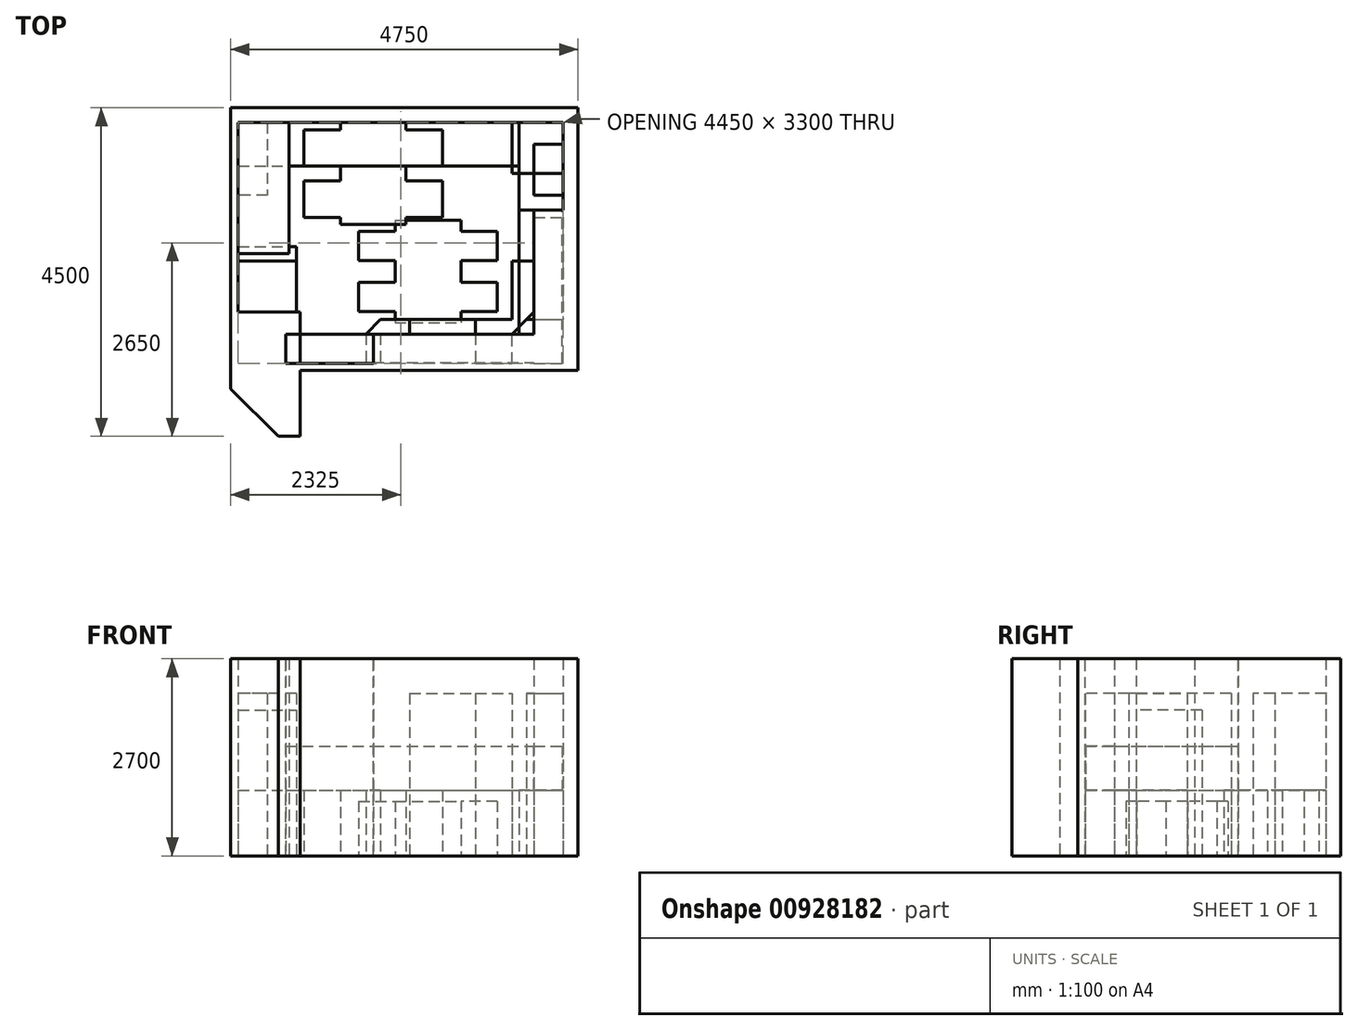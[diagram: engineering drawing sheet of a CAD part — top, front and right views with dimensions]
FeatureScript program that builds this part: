
annotation { "Feature Type Name" : "Feature", "Feature Type Description" : "" }
export const myFeature = defineFeature(function(context is Context, id is Id, definition is map)
    precondition{}
    {
        {
            var Q0;
            Q0=qCreatedBy(makeId("Top.planeOp"),FACE);
            var sketch = newSketch(context, id + "F0", { "sketchPlane" : qUnion([Q0])});
            skLineSegment(sketch, "E0", {"start": v(-2225, 1641.97) * mm, "end": v(2225, 1641.97) * mm});
            skLineSegment(sketch, "E1", {"start": v(2225, 1641.97) * mm, "end": v(2225, -1658.03) * mm});
            skLineSegment(sketch, "E2", {"start": v(-2225, -958.03) * mm, "end": v(-2225, 1641.97) * mm});
            skLineSegment(sketch, "E3.bottom", {"start": v(-2325, 1841.97) * mm, "end": v(2425, 1841.97) * mm});
            skLineSegment(sketch, "E3.left", {"start": v(-2325, 1841.97) * mm, "end": v(-2325, -2008.03) * mm});
            skLineSegment(sketch, "E3.right", {"start": v(2425, 1841.97) * mm, "end": v(2425, -1758.03) * mm});
            skLineSegment(sketch, "E4", {"start": v(-2225, -958.03) * mm, "end": v(-1375, -958.03) * mm});
            skLineSegment(sketch, "E5", {"start": v(-1375, -958.03) * mm, "end": v(-1375, -2658.03) * mm});
            skLineSegment(sketch, "E6", {"start": v(-2325, -2008.03) * mm, "end": v(-1675, -2658.03) * mm});
            skLineSegment(sketch, "E7", {"start": v(-1375, -2658.03) * mm, "end": v(-1675, -2658.03) * mm});
            skLineSegment(sketch, "E8", {"start": v(2425, -1758.03) * mm, "end": v(-1375, -1758.03) * mm});
            skLineSegment(sketch, "E9", {"start": v(2225, -1658.03) * mm, "end": v(-1375, -1658.03) * mm});
            skSolve(sketch);
        }
        {
            var Q0;
            Q0=makeQuery(id+"F0.imprint","IMPRINT",FACE,{"disambiguationData":[TD([[makeQuery(id+"F0.imprint","IMPRINT",EDGE,{"derivedFrom":sQuery(id+"F0.wireOp",EDGE,"E0")}),1.0]])]});
            extrude(context, id + "F1", {"entities" : qUnion([Q0]), "depth" : 2700 * mm, "offsetDistance" : 25 * mm});
        }
        {
            var Q0;
            Q0=makeQuery(id+"F1.opExtrude","SWEPT_FACE",FACE,{"disambiguationData":[OSD([sQuery(id+"F0.wireOp",EDGE,"E0")])]});
            var sketch = newSketch(context, id + "F2", { "sketchPlane" : qUnion([Q0])});
            skLineSegment(sketch, "E10", {"start": v(-2225, 2700) * mm, "end": v(-1525, 2700) * mm});
            skLineSegment(sketch, "E11", {"start": v(-1525, 2700) * mm, "end": v(-1525, 0) * mm});
            skLineSegment(sketch, "E12", {"start": v(-1525, 0) * mm, "end": v(-2225, 0) * mm});
            skLineSegment(sketch, "E13", {"start": v(-2225, 0) * mm, "end": v(-2225, 2700) * mm});
            skSolve(sketch);
        }
        {
            var Q0;
            Q0=makeQuery(id+"F2.imprint","IMPRINT",FACE,{"disambiguationData":[TD([[makeQuery(id+"F2.imprint","IMPRINT",EDGE,{"derivedFrom":sQuery(id+"F2.wireOp",EDGE,"E10")}),-1.0]])]});
            extrude(context, id + "F3", {"entities" : qUnion([Q0]), "depth" : 1800 * mm, "offsetDistance" : 25 * mm});
        }
        {
            var Q0;
            Q0=qCreatedBy(makeId("Top.planeOp"),FACE);
            var sketch = newSketch(context, id + "F4", { "sketchPlane" : qUnion([Q0])});
            skLineSegment(sketch, "E14.bottom", {"start": v(-75, 300) * mm, "end": v(825, 300) * mm});
            skLineSegment(sketch, "E14.left", {"start": v(-75, 300) * mm, "end": v(-75, -1100) * mm});
            skLineSegment(sketch, "E14.right", {"start": v(825, 300) * mm, "end": v(825, -1100) * mm});
            skLineSegment(sketch, "E15", {"start": v(-75, -1100) * mm, "end": v(825, -1100) * mm});
            skLineSegment(sketch, "E16", {"start": v(-75, 150) * mm, "end": v(-575, 150) * mm});
            skLineSegment(sketch, "E17", {"start": v(-575, 150) * mm, "end": v(-575, -250) * mm});
            skLineSegment(sketch, "E18", {"start": v(-575, -250) * mm, "end": v(-75, -250) * mm});
            skLineSegment(sketch, "E19", {"start": v(-75, -550) * mm, "end": v(-575, -550) * mm});
            skLineSegment(sketch, "E20", {"start": v(-575, -550) * mm, "end": v(-575, -950) * mm});
            skLineSegment(sketch, "E21", {"start": v(-575, -950) * mm, "end": v(-75, -950) * mm});
            skLineSegment(sketch, "E22", {"start": v(825, 150) * mm, "end": v(1325, 150) * mm});
            skLineSegment(sketch, "E23", {"start": v(1325, 150) * mm, "end": v(1325, -250) * mm});
            skLineSegment(sketch, "E24", {"start": v(1325, -250) * mm, "end": v(825, -250) * mm});
            skLineSegment(sketch, "E25", {"start": v(825, -550) * mm, "end": v(1325, -550) * mm});
            skLineSegment(sketch, "E26", {"start": v(1325, -550) * mm, "end": v(1325, -950) * mm});
            skLineSegment(sketch, "E27", {"start": v(1325, -950) * mm, "end": v(825, -950) * mm});
            skLineSegment(sketch, "E28", {"start": v(-75, -400) * mm, "end": v(825, -400) * mm});
            skSolve(sketch);
        }
        {
            var Q0;
            {var subQ0=sQuery(id+"F4.wireOp",EDGE,"E16");Q0=makeQuery(id+"F4.imprint","IMPRINT",FACE,{"disambiguationData":[TD([[makeQuery(id+"F4.imprint","IMPRINT",EDGE,{"derivedFrom":subQ0}),1.0]])]});}
            var Q1;
            {var subQ4=sQuery(id+"F4.wireOp",EDGE,"E14.bottom");Q1=makeQuery(id+"F4.imprint","IMPRINT",FACE,{"disambiguationData":[TD([[makeQuery(id+"F4.imprint","IMPRINT",EDGE,{"derivedFrom":subQ4}),-1.0]])]});}
            var Q2;
            {var subQ0=sQuery(id+"F4.wireOp",EDGE,"E22");Q2=makeQuery(id+"F4.imprint","IMPRINT",FACE,{"disambiguationData":[TD([[makeQuery(id+"F4.imprint","IMPRINT",EDGE,{"derivedFrom":subQ0}),-1.0]])]});}
            var Q3;
            {var subQ0=sQuery(id+"F4.wireOp",EDGE,"E15");Q3=makeQuery(id+"F4.imprint","IMPRINT",FACE,{"disambiguationData":[TD([[makeQuery(id+"F4.imprint","IMPRINT",EDGE,{"derivedFrom":subQ0}),1.0]])]});}
            var Q4;
            {var subQ0=sQuery(id+"F4.wireOp",EDGE,"E19");Q4=makeQuery(id+"F4.imprint","IMPRINT",FACE,{"disambiguationData":[TD([[makeQuery(id+"F4.imprint","IMPRINT",EDGE,{"derivedFrom":subQ0}),1.0]])]});}
            var Q5;
            {var subQ0=sQuery(id+"F4.wireOp",EDGE,"E25");Q5=makeQuery(id+"F4.imprint","IMPRINT",FACE,{"disambiguationData":[TD([[makeQuery(id+"F4.imprint","IMPRINT",EDGE,{"derivedFrom":subQ0}),-1.0]])]});}
            extrude(context, id + "F5", {"entities" : qUnion([Q0, Q1, Q2, Q3, Q4, Q5]), "depth" : 750 * mm, "offsetDistance" : 25 * mm});
        }
        {
            var Q0;
            Q0=makeQuery(id+"F1.opExtrude","SWEPT_FACE",FACE,{"disambiguationData":[OSD([sQuery(id+"F0.wireOp",EDGE,"E0")])]});
            var sketch = newSketch(context, id + "F6", { "sketchPlane" : qUnion([Q0])});
            skLineSegment(sketch, "E29.bottom", {"start": v(2225, 900) * mm, "end": v(1625, 900) * mm});
            skLineSegment(sketch, "E29.top", {"start": v(2225, 0) * mm, "end": v(1625, 0) * mm});
            skLineSegment(sketch, "E29.left", {"start": v(2225, 900) * mm, "end": v(2225, 0) * mm});
            skLineSegment(sketch, "E29.right", {"start": v(1625, 900) * mm, "end": v(1625, 0) * mm});
            skSolve(sketch);
        }
        {
            var Q0;
            Q0=makeQuery(id+"F6.imprint","IMPRINT",FACE,{"disambiguationData":[TD([[makeQuery(id+"F6.imprint","IMPRINT",EDGE,{"derivedFrom":sQuery(id+"F6.wireOp",EDGE,"E29.bottom")}),1.0]])]});
            extrude(context, id + "F7", {"entities" : qUnion([Q0]), "depth" : 1200 * mm, "offsetDistance" : 25 * mm});
        }
        {
            var Q0;
            Q0=makeQuery(id+"F7.opExtrude","CAP_FACE",FACE,{"disambiguationData":[OSD([sQuery(id+"F6.wireOp",EDGE,"E29.bottom"),sQuery(id+"F6.wireOp",EDGE,"E29.top"),sQuery(id+"F6.wireOp",EDGE,"E29.left"),sQuery(id+"F6.wireOp",EDGE,"E29.right")])],"isStart":false});
            var sketch = newSketch(context, id + "F8", { "sketchPlane" : qUnion([Q0])});
            skLineSegment(sketch, "E30", {"start": v(2225, 0) * mm, "end": v(2225, 2700) * mm});
            skLineSegment(sketch, "E31", {"start": v(2225, 2700) * mm, "end": v(1825, 2700) * mm});
            skLineSegment(sketch, "E32", {"start": v(1825, 2700) * mm, "end": v(1825, 1500) * mm});
            skLineSegment(sketch, "E33", {"start": v(1825, 1500) * mm, "end": v(2215, 1500) * mm});
            skLineSegment(sketch, "E34", {"start": v(2215, 1500) * mm, "end": v(2215, 900) * mm});
            skLineSegment(sketch, "E35", {"start": v(2215, 900) * mm, "end": v(1625, 900) * mm});
            skLineSegment(sketch, "E36", {"start": v(1625, 900) * mm, "end": v(1625, 0) * mm});
            skLineSegment(sketch, "E37", {"start": v(1625, 0) * mm, "end": v(2225, 0) * mm});
            skSolve(sketch);
        }
        {
            var Q0;
            {var subQ0=sQuery(id+"F8.wireOp",EDGE,"E31");Q0=makeQuery(id+"F8.imprint","IMPRINT",FACE,{"disambiguationData":[TD([[makeQuery(id+"F8.imprint","IMPRINT",EDGE,{"derivedFrom":subQ0}),1.0]])]});}
            var Q1;
            {var subQ1=sQuery(id+"F8.wireOp",EDGE,"E35");Q1=makeQuery(id+"F8.imprint","IMPRINT",FACE,{"disambiguationData":[TD([[makeQuery(id+"F8.imprint","IMPRINT",EDGE,{"derivedFrom":subQ1}),1.0]])]});}
            extrude(context, id + "F9", {"entities" : qUnion([Q0, Q1]), "endBound" : BoundingType.UP_TO_NEXT, "depth" : 25 * mm, "offsetDistance" : 25 * mm});
        }
        {
            var Q0;
            Q0=makeQuery(id+"F9.opExtrude","SWEPT_FACE",FACE,{"disambiguationData":[OSD([sQuery(id+"F8.wireOp",EDGE,"E36")])]});
            var sketch = newSketch(context, id + "F10", { "sketchPlane" : qUnion([Q0])});
            skLineSegment(sketch, "E38", {"start": v(1658.03, 0) * mm, "end": v(1658.03, 2700) * mm});
            skLineSegment(sketch, "E39", {"start": v(1658.03, 2700) * mm, "end": v(1258.03, 2700) * mm});
            skLineSegment(sketch, "E40", {"start": v(1258.03, 2700) * mm, "end": v(1258.03, 1500) * mm});
            skLineSegment(sketch, "E41", {"start": v(1258.03, 1500) * mm, "end": v(1648.03, 1500) * mm});
            skLineSegment(sketch, "E42", {"start": v(1648.03, 1500) * mm, "end": v(1648.03, 900) * mm});
            skLineSegment(sketch, "E43", {"start": v(1648.03, 900) * mm, "end": v(1258.03, 900) * mm});
            skLineSegment(sketch, "E44", {"start": v(1258.03, 900) * mm, "end": v(1258.03, 0) * mm});
            skLineSegment(sketch, "E45", {"start": v(1258.03, 0) * mm, "end": v(1658.03, 0) * mm});
            skSolve(sketch);
        }
        {
            var Q0;
            {var subQ0=sQuery(id+"F10.wireOp",EDGE,"E39");Q0=makeQuery(id+"F10.imprint","IMPRINT",FACE,{"disambiguationData":[TD([[makeQuery(id+"F10.imprint","IMPRINT",EDGE,{"derivedFrom":subQ0}),1.0]])]});}
            var Q1;
            {var subQ1=sQuery(id+"F10.wireOp",EDGE,"E43");Q1=makeQuery(id+"F10.imprint","IMPRINT",FACE,{"disambiguationData":[TD([[makeQuery(id+"F10.imprint","IMPRINT",EDGE,{"derivedFrom":subQ1}),1.0]])]});}
            extrude(context, id + "F11", {"entities" : qUnion([Q0, Q1]), "operationType" : NewBodyOperationType.ADD, "depth" : 2000 * mm, "offsetDistance" : 25 * mm, "hasSecondDirection" : true, "secondDirectionOppositeDirection" : true, "secondDirectionDepth" : 200 * mm});
        }
        {
            var Q0;
            Q0=makeQuery(id+"F11.opExtrude","CAP_FACE",FACE,{"disambiguationData":[OSD([sQuery(id+"F10.wireOp",EDGE,"E38"),sQuery(id+"F10.wireOp",EDGE,"E39"),sQuery(id+"F10.wireOp",EDGE,"E40"),sQuery(id+"F10.wireOp",EDGE,"E41"),sQuery(id+"F10.wireOp",EDGE,"E42"),sQuery(id+"F10.wireOp",EDGE,"E43"),sQuery(id+"F10.wireOp",EDGE,"E44"),sQuery(id+"F10.wireOp",EDGE,"E45")])],"isStart":false});
            var sketch = newSketch(context, id + "F12", { "sketchPlane" : qUnion([Q0])});
            skLineSegment(sketch, "E46.bottom", {"start": v(1658.03, 2700) * mm, "end": v(1258.03, 2700) * mm});
            skLineSegment(sketch, "E46.top", {"start": v(1658.03, 0) * mm, "end": v(1258.03, 0) * mm});
            skLineSegment(sketch, "E46.left", {"start": v(1658.03, 2700) * mm, "end": v(1658.03, 0) * mm});
            skLineSegment(sketch, "E46.right", {"start": v(1258.03, 2700) * mm, "end": v(1258.03, 0) * mm});
            skSolve(sketch);
        }
        {
            var Q0;
            {var subQ4=makeQuery(id+"F11.opExtrude","CAP_EDGE",EDGE,{"disambiguationData":[OSD([sQuery(id+"F10.wireOp",EDGE,"E40")])],"isStart":false});Q0=makeQuery(id+"F12.imprint","IMPRINT",FACE,{"disambiguationData":[TD([[makeQuery(id+"F12.imprint","IMPRINT",EDGE,{"derivedFrom":subQ4}),-1.0]])]});}
            var Q1;
            {var subQ1=sQuery(id+"F12.wireOp",EDGE,"E46.top");Q1=makeQuery(id+"F12.imprint","IMPRINT",FACE,{"disambiguationData":[TD([[makeQuery(id+"F12.imprint","IMPRINT",EDGE,{"derivedFrom":subQ1}),-1.0]])]});}
            extrude(context, id + "F13", {"entities" : qUnion([Q0, Q1]), "depth" : 1200 * mm, "offsetDistance" : 25 * mm});
        }
        {
            var Q0;
            Q0=qCreatedBy(makeId("Top.planeOp"),FACE);
            var sketch = newSketch(context, id + "F14", { "sketchPlane" : qUnion([Q0])});
            skLineSegment(sketch, "E47.bottom", {"start": v(-2225, -58.03) * mm, "end": v(-1425, -58.03) * mm});
            skLineSegment(sketch, "E47.top", {"start": v(-2225, -958.03) * mm, "end": v(-1425, -958.03) * mm});
            skLineSegment(sketch, "E47.left", {"start": v(-2225, -58.03) * mm, "end": v(-2225, -958.03) * mm});
            skLineSegment(sketch, "E47.right", {"start": v(-1425, -58.03) * mm, "end": v(-1425, -958.03) * mm});
            skLineSegment(sketch, "E48.bottom", {"start": v(-2225, 1641.97) * mm, "end": v(1625, 1641.97) * mm});
            skLineSegment(sketch, "E48.top", {"start": v(-2225, 1041.97) * mm, "end": v(1625, 1041.97) * mm});
            skLineSegment(sketch, "E48.left", {"start": v(-2225, 1641.97) * mm, "end": v(-2225, 1041.97) * mm});
            skLineSegment(sketch, "E48.right", {"start": v(1625, 1641.97) * mm, "end": v(1625, 1041.97) * mm});
            skSolve(sketch);
        }
        {
            var Q0;
            Q0=makeQuery(id+"F14.imprint","IMPRINT",FACE,{"disambiguationData":[TD([[makeQuery(id+"F14.imprint","IMPRINT",EDGE,{"derivedFrom":sQuery(id+"F14.wireOp",EDGE,"E48.bottom")}),-1.0]])]});
            extrude(context, id + "F15", {"entities" : qUnion([Q0]), "depth" : 900 * mm, "offsetDistance" : 25 * mm});
        }
        {
            var Q0;
            Q0=makeQuery(id+"F14.imprint","IMPRINT",FACE,{"disambiguationData":[TD([[makeQuery(id+"F14.imprint","IMPRINT",EDGE,{"derivedFrom":sQuery(id+"F14.wireOp",EDGE,"E47.bottom")}),-1.0]])]});
            extrude(context, id + "F16", {"entities" : qUnion([Q0]), "depth" : 2000 * mm, "offsetDistance" : 25 * mm});
        }
        {
            var Q0;
            Q0=qCreatedBy(makeId("Top.planeOp"),FACE);
            var sketch = newSketch(context, id + "F17", { "sketchPlane" : qUnion([Q0])});
            skLineSegment(sketch, "E49.bottom", {"start": v(-275, -1058.03) * mm, "end": v(125, -1058.03) * mm});
            skLineSegment(sketch, "E49.top", {"start": v(-275, -1658.03) * mm, "end": v(125, -1658.03) * mm});
            skLineSegment(sketch, "E49.left", {"start": v(-275, -1058.03) * mm, "end": v(-275, -1658.03) * mm});
            skLineSegment(sketch, "E49.right", {"start": v(125, -1058.03) * mm, "end": v(125, -1658.03) * mm});
            skLineSegment(sketch, "E50.bottom", {"start": v(125, -1058.03) * mm, "end": v(1025, -1058.03) * mm});
            skLineSegment(sketch, "E50.top", {"start": v(125, -1658.03) * mm, "end": v(1025, -1658.03) * mm});
            skLineSegment(sketch, "E50.right", {"start": v(1025, -1058.03) * mm, "end": v(1025, -1658.03) * mm});
            skLineSegment(sketch, "E51.bottom", {"start": v(1025, -1058.03) * mm, "end": v(2225, -1058.03) * mm});
            skLineSegment(sketch, "E51.top", {"start": v(1025, -1658.03) * mm, "end": v(2225, -1658.03) * mm});
            skLineSegment(sketch, "E51.right", {"start": v(2225, -1058.03) * mm, "end": v(2225, -1658.03) * mm});
            skLineSegment(sketch, "E52.bottom", {"start": v(1525, 1641.97) * mm, "end": v(2225, 1641.97) * mm});
            skLineSegment(sketch, "E52.top", {"start": v(1525, -1058.03) * mm, "end": v(2225, -1058.03) * mm});
            skLineSegment(sketch, "E52.left", {"start": v(1525, 1641.97) * mm, "end": v(1525, -1058.03) * mm});
            skLineSegment(sketch, "E52.right", {"start": v(2225, 1641.97) * mm, "end": v(2225, -1058.03) * mm});
            skLineSegment(sketch, "E53", {"start": v(1525, 1341.97) * mm, "end": v(2225, 1341.97) * mm});
            skLineSegment(sketch, "E54", {"start": v(1525, 1441.97) * mm, "end": v(2225, 1441.97) * mm});
            skLineSegment(sketch, "E55.bottom", {"start": v(2225, 1441.97) * mm, "end": v(1825, 1441.97) * mm});
            skLineSegment(sketch, "E55.top", {"start": v(2225, -958.03) * mm, "end": v(1825, -958.03) * mm});
            skLineSegment(sketch, "E55.left", {"start": v(2225, 1441.97) * mm, "end": v(2225, -958.03) * mm});
            skLineSegment(sketch, "E55.right", {"start": v(1825, 1441.97) * mm, "end": v(1825, -958.03) * mm});
            skLineSegment(sketch, "E56.bottom", {"start": v(-275, -1658.03) * mm, "end": v(1525, -1658.03) * mm});
            skLineSegment(sketch, "E56.top", {"start": v(-275, -1258.03) * mm, "end": v(1525, -1258.03) * mm});
            skLineSegment(sketch, "E56.left", {"start": v(-275, -1658.03) * mm, "end": v(-275, -1258.03) * mm});
            skLineSegment(sketch, "E56.right", {"start": v(1525, -1658.03) * mm, "end": v(1525, -1258.03) * mm});
            skLineSegment(sketch, "E57.bottom", {"start": v(-1425, -958.03) * mm, "end": v(-2225, -958.03) * mm});
            skLineSegment(sketch, "E57.top", {"start": v(-1425, -258.03) * mm, "end": v(-2225, -258.03) * mm});
            skLineSegment(sketch, "E57.left", {"start": v(-1425, -958.03) * mm, "end": v(-1425, -258.03) * mm});
            skLineSegment(sketch, "E57.right", {"start": v(-2225, -958.03) * mm, "end": v(-2225, -258.03) * mm});
            skLineSegment(sketch, "E58.bottom", {"start": v(-1825, 1641.97) * mm, "end": v(-2225, 1641.97) * mm});
            skLineSegment(sketch, "E58.top", {"start": v(-1825, 641.97) * mm, "end": v(-2225, 641.97) * mm});
            skLineSegment(sketch, "E58.left", {"start": v(-1825, 1641.97) * mm, "end": v(-1825, 641.97) * mm});
            skLineSegment(sketch, "E58.right", {"start": v(-2225, 1641.97) * mm, "end": v(-2225, 641.97) * mm});
            skLineSegment(sketch, "E59", {"start": v(1825, -958.03) * mm, "end": v(1525, -1258.03) * mm});
            skLineSegment(sketch, "E60", {"start": v(1825, -158.03) * mm, "end": v(2225, -158.03) * mm});
            skPoint(sketch, "E60.endSnap0", {"position": v(2225, 241.97) * mm});
            skLineSegment(sketch, "E61", {"start": v(1825, 641.97) * mm, "end": v(2225, 641.97) * mm});
            skLineSegment(sketch, "E62.bottom", {"start": v(-825, 1641.97) * mm, "end": v(75, 1641.97) * mm});
            skLineSegment(sketch, "E62.top", {"start": v(-825, 241.97) * mm, "end": v(75, 241.97) * mm});
            skLineSegment(sketch, "E62.left", {"start": v(-825, 1641.97) * mm, "end": v(-825, 241.97) * mm});
            skLineSegment(sketch, "E62.right", {"start": v(75, 1641.97) * mm, "end": v(75, 241.97) * mm});
            skLineSegment(sketch, "E63.bottom", {"start": v(-1325, 1541.97) * mm, "end": v(575, 1541.97) * mm});
            skLineSegment(sketch, "E63.top", {"start": v(-1325, 1041.97) * mm, "end": v(575, 1041.97) * mm});
            skLineSegment(sketch, "E63.left", {"start": v(-1325, 1541.97) * mm, "end": v(-1325, 1041.97) * mm});
            skLineSegment(sketch, "E63.right", {"start": v(575, 1541.97) * mm, "end": v(575, 1041.97) * mm});
            skLineSegment(sketch, "E64.bottom", {"start": v(-1325, 841.97) * mm, "end": v(575, 841.97) * mm});
            skLineSegment(sketch, "E64.top", {"start": v(-1325, 341.97) * mm, "end": v(575, 341.97) * mm});
            skLineSegment(sketch, "E64.left", {"start": v(-1325, 841.97) * mm, "end": v(-1325, 341.97) * mm});
            skLineSegment(sketch, "E64.right", {"start": v(575, 841.97) * mm, "end": v(575, 341.97) * mm});
            skLineSegment(sketch, "E65", {"start": v(-275, -1058.03) * mm, "end": v(-475, -1258.03) * mm});
            skLineSegment(sketch, "E66", {"start": v(-475, -1258.03) * mm, "end": v(-475, -1658.03) * mm});
            skLineSegment(sketch, "E67", {"start": v(-475, -1658.03) * mm, "end": v(-275, -1658.03) * mm});
            skLineSegment(sketch, "E68", {"start": v(-825, 941.97) * mm, "end": v(75, 941.97) * mm});
            skLineSegment(sketch, "E69", {"start": v(-375, 1641.97) * mm, "end": v(-375, 241.97) * mm});
            skLineSegment(sketch, "E70", {"start": v(1525, -258.03) * mm, "end": v(2225, -258.03) * mm});
            skLineSegment(sketch, "E71.bottom", {"start": v(1525, 941.97) * mm, "end": v(2225, 941.97) * mm});
            skLineSegment(sketch, "E71.top", {"start": v(1525, 341.97) * mm, "end": v(2225, 341.97) * mm});
            skLineSegment(sketch, "E71.left", {"start": v(1525, 941.97) * mm, "end": v(1525, 341.97) * mm});
            skLineSegment(sketch, "E71.right", {"start": v(2225, 941.97) * mm, "end": v(2225, 341.97) * mm});
            skSolve(sketch);
        }
        {
            var Q0;
            {var subQ5=sQuery(id+"F17.wireOp",EDGE,"E56.left");Q0=makeQuery(id+"F17.imprint","IMPRINT",FACE,{"disambiguationData":[TD([[makeQuery(id+"F17.imprint","IMPRINT",EDGE,{"derivedFrom":subQ5}),-1.0]])]});}
            var Q1;
            {var subQ0=sQuery(id+"F17.wireOp",EDGE,"E56.bottom");var subQ1=sQuery(id+"F17.wireOp",EDGE,"E49.right");var subQ2=makeQuery(id+"F17.imprint","INTERSECT",VERTEX,{"derivedFrom":[subQ1,subQ0]});Q1=makeQuery(id+"F17.imprint","IMPRINT",FACE,{"disambiguationData":[TD([[makeQuery(id+"F17.imprint","IMPRINT",EDGE,{"disambiguationData":[TD([[subQ2,1.0]])],"derivedFrom":subQ1}),1.0]])]});}
            var Q2;
            {var subQ5=sQuery(id+"F17.wireOp",EDGE,"E56.right");Q2=makeQuery(id+"F17.imprint","IMPRINT",FACE,{"disambiguationData":[TD([[makeQuery(id+"F17.imprint","IMPRINT",EDGE,{"derivedFrom":subQ5}),1.0]])]});}
            var Q3;
            Q3=makeQuery(id+"F17.imprint","IMPRINT",FACE,{"disambiguationData":[TD([[makeQuery(id+"F17.imprint","IMPRINT",EDGE,{"derivedFrom":sQuery(id+"F17.wireOp",EDGE,"E51.top")}),1.0]])]});
            var Q4;
            {var subQ5=sQuery(id+"F17.wireOp",EDGE,"E55.top");Q4=makeQuery(id+"F17.imprint","IMPRINT",FACE,{"disambiguationData":[TD([[makeQuery(id+"F17.imprint","IMPRINT",EDGE,{"derivedFrom":subQ5}),1.0]])]});}
            var Q5;
            {var subQ0=sQuery(id+"F17.wireOp",EDGE,"E55.top");Q5=makeQuery(id+"F17.imprint","IMPRINT",FACE,{"disambiguationData":[TD([[makeQuery(id+"F17.imprint","IMPRINT",EDGE,{"derivedFrom":subQ0}),-1.0]])]});}
            var Q6;
            {var subQ0=sQuery(id+"F17.wireOp",EDGE,"E60");Q6=makeQuery(id+"F17.imprint","IMPRINT",FACE,{"disambiguationData":[TD([[makeQuery(id+"F17.imprint","IMPRINT",EDGE,{"derivedFrom":subQ0}),-1.0]])]});}
            var Q7;
            {var subQ0=sQuery(id+"F17.wireOp",EDGE,"E60");Q7=makeQuery(id+"F17.imprint","IMPRINT",FACE,{"disambiguationData":[TD([[makeQuery(id+"F17.imprint","IMPRINT",EDGE,{"derivedFrom":subQ0}),1.0]])]});}
            var Q8;
            {var subQ5=sQuery(id+"F17.wireOp",EDGE,"E61");Q8=makeQuery(id+"F17.imprint","IMPRINT",FACE,{"disambiguationData":[TD([[makeQuery(id+"F17.imprint","IMPRINT",EDGE,{"derivedFrom":subQ5}),1.0]])]});}
            var Q9;
            {var subQ5=sQuery(id+"F17.wireOp",EDGE,"E55.bottom");Q9=makeQuery(id+"F17.imprint","IMPRINT",FACE,{"disambiguationData":[TD([[makeQuery(id+"F17.imprint","IMPRINT",EDGE,{"derivedFrom":subQ5}),1.0]])]});}
            var Q10;
            Q10=makeQuery(id+"F17.imprint","IMPRINT",FACE,{"disambiguationData":[TD([[makeQuery(id+"F17.imprint","IMPRINT",EDGE,{"derivedFrom":sQuery(id+"F17.wireOp",EDGE,"E57.bottom")}),-1.0]])]});
            var Q11;
            Q11=makeQuery(id+"F17.imprint","IMPRINT",FACE,{"disambiguationData":[TD([[makeQuery(id+"F17.imprint","IMPRINT",EDGE,{"derivedFrom":sQuery(id+"F17.wireOp",EDGE,"E58.bottom")}),1.0]])]});
            extrude(context, id + "F18", {"entities" : qUnion([Q0, Q1, Q2, Q3, Q4, Q5, Q6, Q7, Q8, Q9, Q10, Q11]), "depth" : 2225 * mm, "offsetDistance" : 25 * mm});
        }
        {
            var Q0;
            {var subQ5=sQuery(id+"F17.wireOp",EDGE,"E63.left");Q0=makeQuery(id+"F17.imprint","IMPRINT",FACE,{"disambiguationData":[TD([[makeQuery(id+"F17.imprint","IMPRINT",EDGE,{"derivedFrom":subQ5}),1.0]])]});}
            var Q1;
            {var subQ0=sQuery(id+"F17.wireOp",EDGE,"E62.left");var subQ1=sQuery(id+"F17.wireOp",EDGE,"E62.bottom");var subQ2=makeQuery(id+"F17.imprint","INTERSECT",VERTEX,{"derivedFrom":[subQ1,subQ0]});Q1=makeQuery(id+"F17.imprint","IMPRINT",FACE,{"disambiguationData":[TD([[makeQuery(id+"F17.imprint","IMPRINT",EDGE,{"disambiguationData":[TD([[subQ2,-1.0]])],"derivedFrom":subQ1}),-1.0]])]});}
            var Q2;
            {var subQ0=sQuery(id+"F17.wireOp",EDGE,"E62.right");var subQ1=sQuery(id+"F17.wireOp",EDGE,"E62.bottom");var subQ2=makeQuery(id+"F17.imprint","INTERSECT",VERTEX,{"derivedFrom":[subQ1,subQ0]});Q2=makeQuery(id+"F17.imprint","IMPRINT",FACE,{"disambiguationData":[TD([[makeQuery(id+"F17.imprint","IMPRINT",EDGE,{"disambiguationData":[TD([[subQ2,1.0]])],"derivedFrom":subQ1}),-1.0]])]});}
            var Q3;
            {var subQ0=sQuery(id+"F17.wireOp",EDGE,"E63.bottom");var subQ1=sQuery(id+"F17.wireOp",EDGE,"E62.right");var subQ2=makeQuery(id+"F17.imprint","INTERSECT",VERTEX,{"derivedFrom":[subQ1,subQ0]});Q3=makeQuery(id+"F17.imprint","IMPRINT",FACE,{"disambiguationData":[TD([[makeQuery(id+"F17.imprint","IMPRINT",EDGE,{"disambiguationData":[TD([[subQ2,-1.0]])],"derivedFrom":subQ1}),-1.0]])]});}
            var Q4;
            {var subQ5=sQuery(id+"F17.wireOp",EDGE,"E63.right");Q4=makeQuery(id+"F17.imprint","IMPRINT",FACE,{"disambiguationData":[TD([[makeQuery(id+"F17.imprint","IMPRINT",EDGE,{"derivedFrom":subQ5}),-1.0]])]});}
            var Q5;
            {var subQ0=sQuery(id+"F17.wireOp",EDGE,"E63.bottom");var subQ1=sQuery(id+"F17.wireOp",EDGE,"E62.left");var subQ2=makeQuery(id+"F17.imprint","INTERSECT",VERTEX,{"derivedFrom":[subQ1,subQ0]});Q5=makeQuery(id+"F17.imprint","IMPRINT",FACE,{"disambiguationData":[TD([[makeQuery(id+"F17.imprint","IMPRINT",EDGE,{"disambiguationData":[TD([[subQ2,-1.0]])],"derivedFrom":subQ1}),1.0]])]});}
            var Q6;
            {var subQ5=sQuery(id+"F17.wireOp",EDGE,"E64.left");Q6=makeQuery(id+"F17.imprint","IMPRINT",FACE,{"disambiguationData":[TD([[makeQuery(id+"F17.imprint","IMPRINT",EDGE,{"derivedFrom":subQ5}),1.0]])]});}
            var Q7;
            {var subQ0=sQuery(id+"F17.wireOp",EDGE,"E64.bottom");var subQ1=sQuery(id+"F17.wireOp",EDGE,"E62.left");var subQ2=makeQuery(id+"F17.imprint","INTERSECT",VERTEX,{"derivedFrom":[subQ1,subQ0]});Q7=makeQuery(id+"F17.imprint","IMPRINT",FACE,{"disambiguationData":[TD([[makeQuery(id+"F17.imprint","IMPRINT",EDGE,{"disambiguationData":[TD([[subQ2,-1.0]])],"derivedFrom":subQ1}),1.0]])]});}
            var Q8;
            {var subQ0=sQuery(id+"F17.wireOp",EDGE,"E62.left");var subQ1=sQuery(id+"F17.wireOp",EDGE,"E62.top");var subQ2=makeQuery(id+"F17.imprint","INTERSECT",VERTEX,{"derivedFrom":[subQ1,subQ0]});Q8=makeQuery(id+"F17.imprint","IMPRINT",FACE,{"disambiguationData":[TD([[makeQuery(id+"F17.imprint","IMPRINT",EDGE,{"disambiguationData":[TD([[subQ2,-1.0]])],"derivedFrom":subQ1}),1.0]])]});}
            var Q9;
            {var subQ0=sQuery(id+"F17.wireOp",EDGE,"E68");var subQ1=sQuery(id+"F17.wireOp",EDGE,"E62.right");var subQ2=makeQuery(id+"F17.imprint","INTERSECT",VERTEX,{"derivedFrom":[subQ1,subQ0]});Q9=makeQuery(id+"F17.imprint","IMPRINT",FACE,{"disambiguationData":[TD([[makeQuery(id+"F17.imprint","IMPRINT",EDGE,{"disambiguationData":[TD([[subQ2,1.0]])],"derivedFrom":subQ1}),-1.0]])]});}
            var Q10;
            {var subQ0=sQuery(id+"F17.wireOp",EDGE,"E68");var subQ1=sQuery(id+"F17.wireOp",EDGE,"E62.left");var subQ2=makeQuery(id+"F17.imprint","INTERSECT",VERTEX,{"derivedFrom":[subQ1,subQ0]});Q10=makeQuery(id+"F17.imprint","IMPRINT",FACE,{"disambiguationData":[TD([[makeQuery(id+"F17.imprint","IMPRINT",EDGE,{"disambiguationData":[TD([[subQ2,-1.0]])],"derivedFrom":subQ1}),1.0]])]});}
            var Q11;
            {var subQ0=sQuery(id+"F17.wireOp",EDGE,"E68");var subQ1=sQuery(id+"F17.wireOp",EDGE,"E62.left");var subQ2=makeQuery(id+"F17.imprint","INTERSECT",VERTEX,{"derivedFrom":[subQ1,subQ0]});Q11=makeQuery(id+"F17.imprint","IMPRINT",FACE,{"disambiguationData":[TD([[makeQuery(id+"F17.imprint","IMPRINT",EDGE,{"disambiguationData":[TD([[subQ2,1.0]])],"derivedFrom":subQ1}),1.0]])]});}
            var Q12;
            {var subQ1=sQuery(id+"F17.wireOp",EDGE,"E52.bottom");Q12=makeQuery(id+"F17.imprint","IMPRINT",FACE,{"disambiguationData":[TD([[makeQuery(id+"F17.imprint","IMPRINT",EDGE,{"derivedFrom":subQ1}),-1.0]])]});}
            var Q13;
            {var subQ3=sQuery(id+"F17.wireOp",EDGE,"E54");Q13=makeQuery(id+"F17.imprint","IMPRINT",FACE,{"disambiguationData":[TD([[makeQuery(id+"F17.imprint","IMPRINT",EDGE,{"derivedFrom":subQ3}),-1.0]])]});}
            var Q14;
            {var subQ3=sQuery(id+"F17.wireOp",EDGE,"E53");var subQ4=sQuery(id+"F17.wireOp",EDGE,"E52.left");var subQ5=makeQuery(id+"F17.imprint","INTERSECT",VERTEX,{"derivedFrom":[subQ4,subQ3]});Q14=makeQuery(id+"F17.imprint","IMPRINT",FACE,{"disambiguationData":[TD([[makeQuery(id+"F17.imprint","IMPRINT",EDGE,{"disambiguationData":[TD([[subQ5,-1.0]])],"derivedFrom":subQ4}),1.0]])]});}
            var Q15;
            {var subQ0=sQuery(id+"F17.wireOp",EDGE,"E68");var subQ1=sQuery(id+"F17.wireOp",EDGE,"E62.right");var subQ2=makeQuery(id+"F17.imprint","INTERSECT",VERTEX,{"derivedFrom":[subQ1,subQ0]});Q15=makeQuery(id+"F17.imprint","IMPRINT",FACE,{"disambiguationData":[TD([[makeQuery(id+"F17.imprint","IMPRINT",EDGE,{"disambiguationData":[TD([[subQ2,-1.0]])],"derivedFrom":subQ1}),-1.0]])]});}
            var Q16;
            {var subQ0=sQuery(id+"F17.wireOp",EDGE,"E64.bottom");var subQ1=sQuery(id+"F17.wireOp",EDGE,"E62.right");var subQ2=makeQuery(id+"F17.imprint","INTERSECT",VERTEX,{"derivedFrom":[subQ1,subQ0]});Q16=makeQuery(id+"F17.imprint","IMPRINT",FACE,{"disambiguationData":[TD([[makeQuery(id+"F17.imprint","IMPRINT",EDGE,{"disambiguationData":[TD([[subQ2,-1.0]])],"derivedFrom":subQ1}),-1.0]])]});}
            var Q17;
            {var subQ5=sQuery(id+"F17.wireOp",EDGE,"E64.right");Q17=makeQuery(id+"F17.imprint","IMPRINT",FACE,{"disambiguationData":[TD([[makeQuery(id+"F17.imprint","IMPRINT",EDGE,{"derivedFrom":subQ5}),-1.0]])]});}
            var Q18;
            {var subQ0=sQuery(id+"F17.wireOp",EDGE,"E62.right");var subQ1=sQuery(id+"F17.wireOp",EDGE,"E62.top");var subQ2=makeQuery(id+"F17.imprint","INTERSECT",VERTEX,{"derivedFrom":[subQ1,subQ0]});Q18=makeQuery(id+"F17.imprint","IMPRINT",FACE,{"disambiguationData":[TD([[makeQuery(id+"F17.imprint","IMPRINT",EDGE,{"disambiguationData":[TD([[subQ2,1.0]])],"derivedFrom":subQ1}),1.0]])]});}
            var Q19;
            {var subQ5=sQuery(id+"F17.wireOp",EDGE,"E70");var subQ7=sQuery(id+"F17.wireOp",EDGE,"E52.left");var subQ9=makeQuery(id+"F17.imprint","INTERSECT",VERTEX,{"derivedFrom":[subQ7,subQ5]});Q19=makeQuery(id+"F17.imprint","IMPRINT",FACE,{"disambiguationData":[TD([[makeQuery(id+"F17.imprint","IMPRINT",EDGE,{"disambiguationData":[TD([[subQ9,-1.0]])],"derivedFrom":subQ5}),-1.0]])]});}
            var Q20;
            {var subQ6=sQuery(id+"F17.wireOp",EDGE,"E51.bottom");Q20=makeQuery(id+"F17.imprint","IMPRINT",FACE,{"disambiguationData":[TD([[makeQuery(id+"F17.imprint","IMPRINT",EDGE,{"derivedFrom":subQ6}),-1.0]])]});}
            var Q21;
            {var subQ0=sQuery(id+"F17.wireOp",EDGE,"E50.bottom");Q21=makeQuery(id+"F17.imprint","IMPRINT",FACE,{"disambiguationData":[TD([[makeQuery(id+"F17.imprint","IMPRINT",EDGE,{"derivedFrom":subQ0}),-1.0]])]});}
            var Q22;
            {var subQ0=sQuery(id+"F17.wireOp",EDGE,"E49.bottom");Q22=makeQuery(id+"F17.imprint","IMPRINT",FACE,{"disambiguationData":[TD([[makeQuery(id+"F17.imprint","IMPRINT",EDGE,{"derivedFrom":subQ0}),-1.0]])]});}
            var Q23;
            Q23=makeQuery(id+"F17.imprint","IMPRINT",FACE,{"disambiguationData":[TD([[makeQuery(id+"F17.imprint","IMPRINT",EDGE,{"derivedFrom":sQuery(id+"F17.wireOp",EDGE,"E49.left")}),-1.0]])]});
            extrude(context, id + "F19", {"entities" : qUnion([Q0, Q1, Q2, Q3, Q4, Q5, Q6, Q7, Q8, Q9, Q10, Q11, Q12, Q13, Q14, Q15, Q16, Q17, Q18, Q19, Q20, Q21, Q22, Q23]), "depth" : 900 * mm, "offsetDistance" : 25 * mm});
        }
    });
